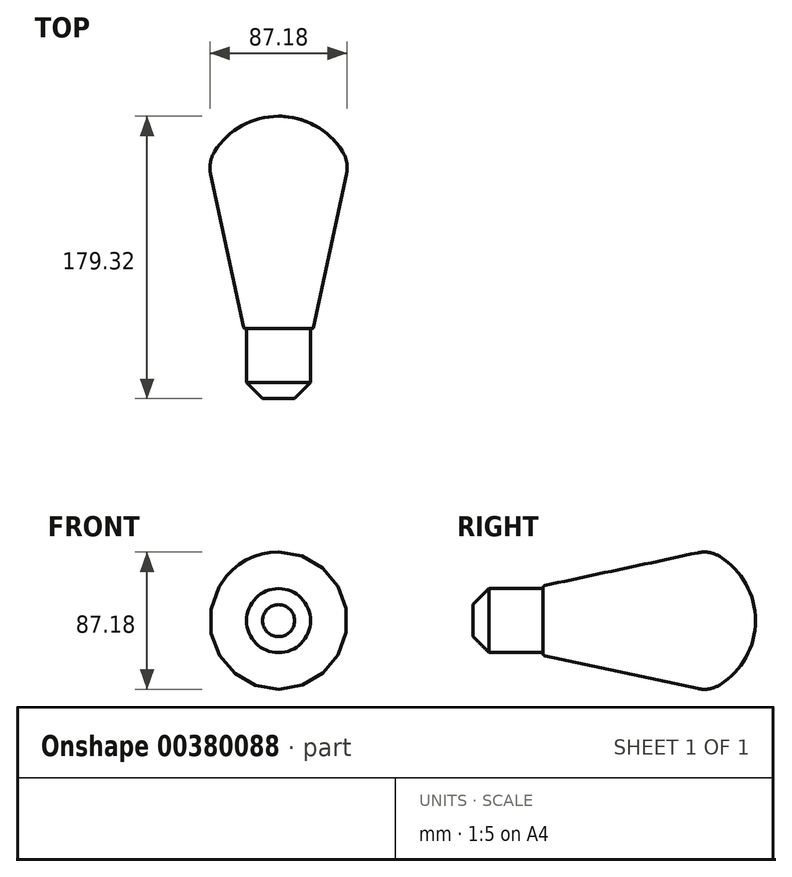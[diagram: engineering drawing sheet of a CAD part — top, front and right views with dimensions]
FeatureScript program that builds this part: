
annotation { "Feature Type Name" : "Feature", "Feature Type Description" : "" }
export const myFeature = defineFeature(function(context is Context, id is Id, definition is map)
    precondition{}
    {
        {
            var Q0;
            Q0=qCreatedBy(makeId("Top.planeOp"),FACE);
            var sketch = newSketch(context, id + "F0", { "sketchPlane" : qUnion([Q0])});
            skLineSegment(sketch, "E0", {"start": v(0, 134.87) * mm, "end": v(0, 0) * mm, "construction": true});
            skLineSegment(sketch, "E1", {"start": v(0, 0) * mm, "end": v(21.07, 0) * mm});
            skLineSegment(sketch, "E2", {"start": v(22.31, 1) * mm, "end": v(43.16, 98.22) * mm});
            skArc(sketch, "E3", {"start": v(40.7, 112.3) * mm, "mid": v(23.27, 128.85) * mm, "end": v(0, 134.87) * mm});
            skPoint(sketch, "E4.visualSharp", {"position": v(22.1, 0) * mm});
            skArc(sketch, "E4.filletArc", {"start": v(21.07, 0) * mm, "mid": v(21.87, 0.28) * mm, "end": v(22.31, 1) * mm});
            skPoint(sketch, "E5.visualSharp", {"position": v(33.34, 52.4) * mm});
            skArc(sketch, "E5.filletArc", {"start": v(43.16, 98.22) * mm, "mid": v(43.3, 105.5) * mm, "end": v(40.7, 112.3) * mm});
            skLineSegment(sketch, "E6", {"start": v(0, 134.87) * mm, "end": v(0, 0) * mm});
            skLineSegment(sketch, "E7", {"start": v(0, 134.87) * mm, "end": v(23.71, 134.87) * mm, "construction": true});
            skSolve(sketch);
        }
        {
            var Q0;
            Q0=makeQuery(id+"F0.imprint","IMPRINT",FACE,{"disambiguationData":[TD([[makeQuery(id+"F0.imprint","IMPRINT",EDGE,{"derivedFrom":sQuery(id+"F0.wireOp",EDGE,"E1")}),1.0]])]});
            var Q1;
            Q1=sQuery(id+"F0.wireOp",EDGE,"E6");
            revolve(context, id + "F1", {"entities" : qUnion([Q0]), "axis" : qUnion([Q1]), "revolveType" : RevolveType.FULL});
        }
        {
            var Q0;
            Q0=makeQuery(id+"F1.opRevolve","SWEPT_FACE",FACE,{"disambiguationData":[OSD([sQuery(id+"F0.wireOp",EDGE,"E1")])]});
            var sketch = newSketch(context, id + "F2", { "sketchPlane" : qUnion([Q0])});
            skCircle(sketch, "E8", {"center": v(0, 0) * mm, "radius": 20.32 * mm});
            skSolve(sketch);
        }
        {
            var Q0;
            Q0=makeQuery(id+"F2.imprint","IMPRINT",FACE,{"disambiguationData":[TD([[makeQuery(id+"F2.imprint","IMPRINT",EDGE,{"derivedFrom":sQuery(id+"F2.wireOp",EDGE,"E8")}),1.0]])]});
            extrude(context, id + "F3", {"entities" : qUnion([Q0]), "operationType" : NewBodyOperationType.ADD, "depth" : 44.45 * mm});
        }
        {
            var Q0;
            Q0=makeQuery(id+"F3.opExtrude","CAP_EDGE",EDGE,{"disambiguationData":[OSD([sQuery(id+"F2.wireOp",EDGE,"E8")])],"isStart":false});
            chamfer(context, id + "F4", {"entities" : qUnion([Q0]), "width" : 10.16 * mm, "tangentPropagation" : true});
        }
    });
